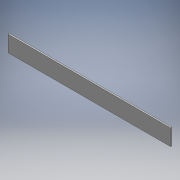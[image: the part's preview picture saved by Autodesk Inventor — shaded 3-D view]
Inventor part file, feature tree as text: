
AUTODESK INVENTOR PART (.ipt)
format: ipt  version: 2016 (Build 200138000, 138)  size: 91,136 bytes
history: native  units: mm
features: extrude x1, sketch x1
ambient origin geometry x8: Origin, YZ Plane, XZ Plane, XY Plane, X Axis, Y Axis, Z Axis, Center Point
bodies: Solid1 (feature_tree)
feature tree (2):
  extrude  "Extrusion1"  Depth=800.0mm
  sketch  "Sketch1"  dims[d0=80.0mm d1=800.0mm d2=6.0mm d3=0.0mm]
